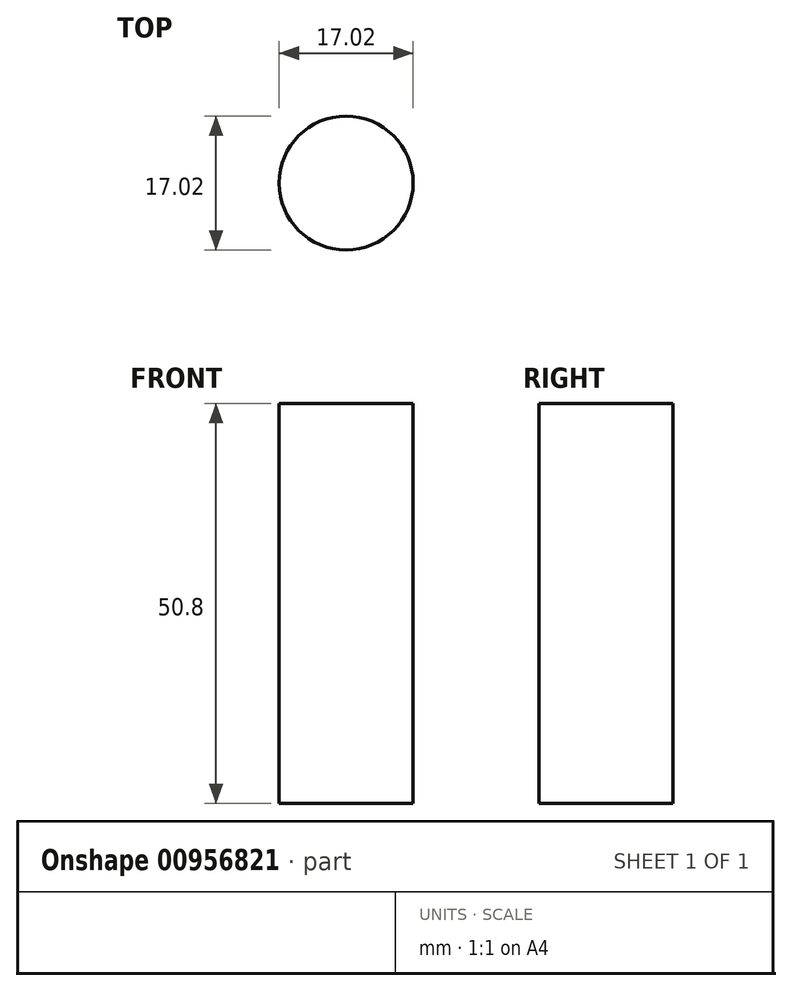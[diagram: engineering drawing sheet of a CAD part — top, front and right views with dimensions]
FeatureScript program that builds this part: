
annotation { "Feature Type Name" : "Feature", "Feature Type Description" : "" }
export const myFeature = defineFeature(function(context is Context, id is Id, definition is map)
    precondition{}
    {
        {
            var Q0;
            Q0=qCreatedBy(makeId("Top.planeOp"),FACE);
            var sketch = newSketch(context, id + "F0", { "sketchPlane" : qUnion([Q0])});
            skCircle(sketch, "E0", {"center": v(1.88, 0) * mm, "radius": 8.5 * mm});
            skSolve(sketch);
        }
        {
            var Q0;
            Q0=makeQuery(id+"F0.imprint","IMPRINT",FACE,{"disambiguationData":[TD([[makeQuery(id+"F0.imprint","IMPRINT",EDGE,{"derivedFrom":sQuery(id+"F0.wireOp",EDGE,"E0")}),1.0]])]});
            extrude(context, id + "F1", {"entities" : qUnion([Q0]), "depth" : 50.8 * mm, "offsetDistance" : 25.4 * mm});
        }
    });
